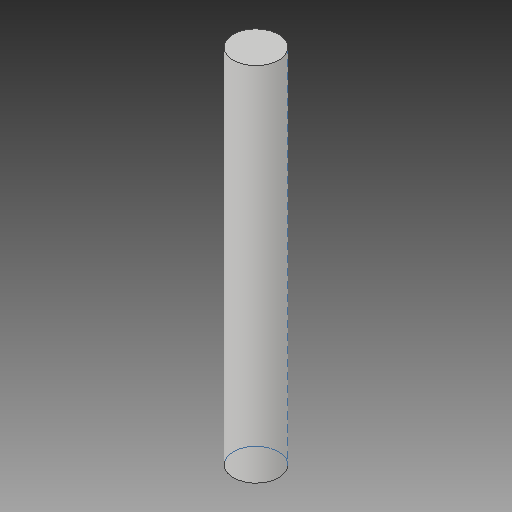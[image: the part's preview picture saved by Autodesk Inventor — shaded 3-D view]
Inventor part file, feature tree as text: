
AUTODESK INVENTOR PART (.ipt)
format: ipt  version: 2019 (Build 230136000, 136)  size: 91,136 bytes
history: native  units: in
note: dims shown in document units (in); Inventor stores cm internally (conversion verified against a paired STEP export)
features: extrude x1, sketch x1
ambient origin geometry x8: Origin, YZ Plane, XZ Plane, XY Plane, X Axis, Y Axis, Z Axis, Center Point
bodies: Solid1 (feature_tree)
feature tree (2):
  extrude  "Extrusion1"  Depth=3.0in TaperAngle=0.0deg
  sketch  "Sketch1"  dims[d0=0.375in d1=3.0in d2=0.0in]
